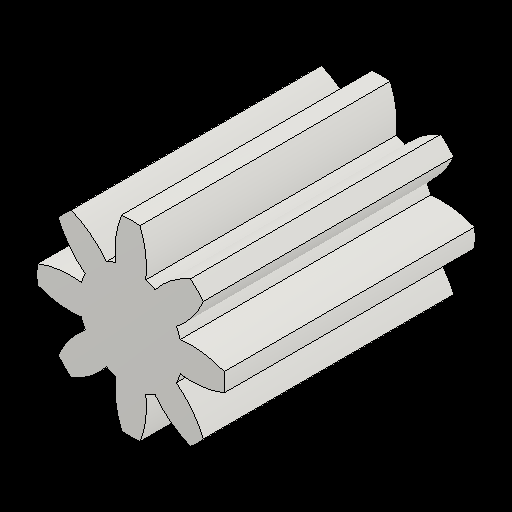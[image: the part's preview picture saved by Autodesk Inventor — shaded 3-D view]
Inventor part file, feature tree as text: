
AUTODESK INVENTOR PART (.ipt)
format: ipt  version: 2023.2 (Build 272271030, 271C)  size: 178,176 bytes
history: native  units: mm (DEFAULTED — no unit token found)
features: plane x3, other x3, sketch x2, extrude x1
ambient origin geometry x8: Origin, YZ Plane, XZ Plane, XY Plane, X Axis, Y Axis, Z Axis, Center Point
bodies: Solid1 (feature_tree)
feature tree (9):
  extrude  "Extrusion1"  Depth=20.0mm TaperAngle=0.0deg
  plane  "Work Plane2"
  plane  "Work Plane8"
  plane  "Work Plane9"
  other  "Spur Gear"
  sketch  "Sketch1"  dims[d0=15.0mm d1=20.0mm d2=0.0mm]
  sketch  "Sketch2"  dims[d3=12.0mm d4=10.0mm d5=0.0mm d16=12.0mm d17=0.0mm d34=22.5deg d39=0.0mm d41=0.0mm d43=12.0mm d46=12.0mm d47=0.0mm d48=0.0mm]
  other  "Srf1"
  other  "Pitch Diameter"
